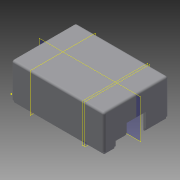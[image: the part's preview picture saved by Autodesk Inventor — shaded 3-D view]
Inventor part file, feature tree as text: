
AUTODESK INVENTOR PART (.ipt)
format: ipt  version: 2015 (Build 190159000, 159)  size: 255,488 bytes
history: native  units: in
note: dims shown in document units (in); Inventor stores cm internally (conversion verified against a paired STEP export)
features: sketch x10, extrude x5, plane x4, rib x3, fillet x2, hole x1, mirror x1
ambient origin geometry x8: Origin, YZ Plane, XZ Plane, XY Plane, X Axis, Y Axis, Z Axis, Center Point
bodies: Solid1 (feature_tree)
feature tree (26):
  extrude  "Extrusion1"  Depth=2.5197in
  extrude  "Extrusion2"  Depth=0.0984in
  fillet  "Fillet1"  Radius=0.0984in
  sketch  "Sketch4"  dims[d7=0.0984in d8=1.2795in d9=0.0in]
  extrude  "Extrusion4"  Depth=1.2795in TaperAngle=0.0deg
  extrude  "Extrusion5"  Depth=0.0787in
  hole  "Hole1"  [1 undecoded]
  extrude  "Extrusion6"  Depth=0.3346in
  fillet  "Fillet2"  [1 undecoded]
  sketch  "Sketch10"  dims[d25=0.1969in]
  plane  "Work Plane1"
  rib  "Rib1"
  plane  "Work Plane2"
  mirror  "Mirror1"
  plane  "Work Plane4"
  rib  "Rib2"
  plane  "Work Plane5"
  rib  "Rib3"
  sketch  "Sketch2"  dims[d2=3.622in d3=2.5197in]
  sketch  "Sketch3"  dims[d4=0.0984in d5=0.0984in d6=0.0984in]
  sketch  "Sketch6"  dims[d10=0.0591in d11=0.0in d12=0.0787in]
  sketch  "Sketch8"  dims[d17=0.2362in d18=0.2362in]
  sketch  "Sketch9"  dims[d22=0.1969in d23=0.3346in d24=0.0in]
  sketch  "Sketch12"  dims[d26=0.3346in]
  sketch  "Sketch14"  dims[d27=0.0in]
  sketch  "Sketch15"  dims[d28=0.1969in d29=0.3346in d30=0.0in d31=0.0984in d33=0.0984in d34=0.1969in d35=0.3346in d36=0.0in d37=0.0984in d38=0.0984in d39=0.0787in d40=0.0984in d43=0.0984in d44=0.0in d45=0.2756in d46=0.0in d47=0.1181in d48=0.0984in d49=0.1181in d50=0.0984in d51=0.1181in d52=0.1181in d53=0.315in d54=0.0984in d55=0.315in d56=0.315in d57=0.0984in d58=0.315in d59=0.1181in d60=0.2362in d61=0.1575in d62=0.0787in d63=90.0deg d64=0.1969in d65=0.0in d66=0.7874in d67=0.3543in d68=0.6693in d69=0.4331in d70=0.3937in d71=0.1969in d72=0.0in d73=0.0787in d74=0.6496in d77=0.0394in d78=0.1969in d79=0.0in d80=0.0in d81=0.0394in d82=0.0394in d86=0.6496in d88=0.7283in d89=0.6496in d90=0.7283in d91=0.0394in d92=0.1969in d93=0.0in d94=0.0in d95=0.0394in d96=0.0394in d97=135.0deg d98=45.0deg d99=0.6496in d101=45.0deg d102=0.0394in d103=0.1969in d104=0.0in d105=0.0in d106=0.0394in d107=0.0394in]
note: 2 required parameter values undecoded (feature->parameter linkage not recoverable at this tier; creation-order binding heuristic only, values carry confidence <= 0.55)
